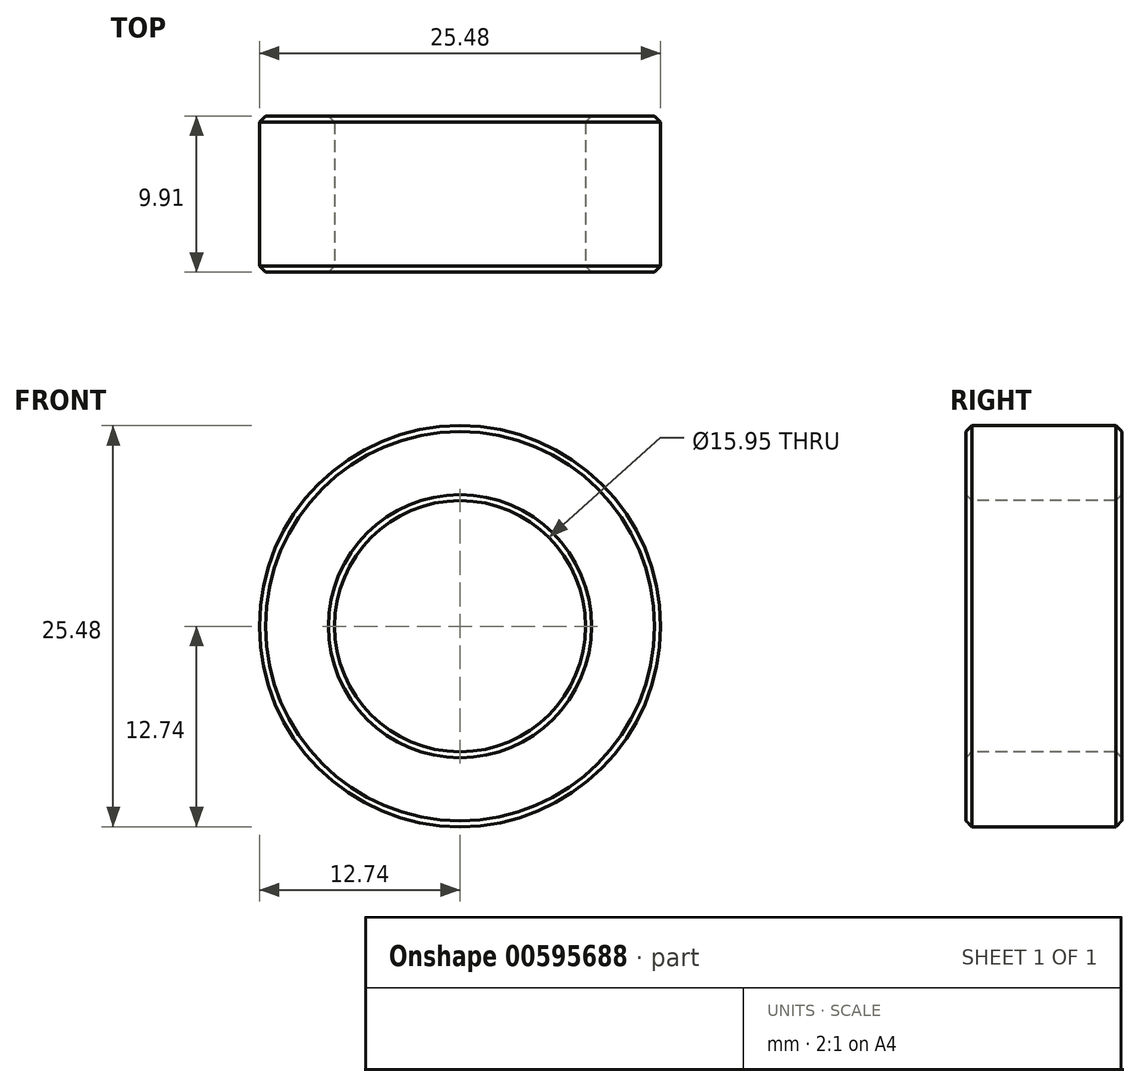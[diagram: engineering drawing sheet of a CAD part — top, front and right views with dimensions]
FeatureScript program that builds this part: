
annotation { "Feature Type Name" : "Feature", "Feature Type Description" : "" }
export const myFeature = defineFeature(function(context is Context, id is Id, definition is map)
    precondition{}
    {
        {
            var Q0;
            Q0=qCreatedBy(makeId("Right.planeOp"),FACE);
            var sketch = newSketch(context, id + "F0", { "sketchPlane" : qUnion([Q0])});
            skLineSegment(sketch, "E0.bottom", {"start": v(0, 7.98) * mm, "end": v(9.9, 7.98) * mm});
            skLineSegment(sketch, "E0.top", {"start": v(0, 12.74) * mm, "end": v(9.9, 12.74) * mm});
            skLineSegment(sketch, "E0.left", {"start": v(0, 7.98) * mm, "end": v(0, 12.74) * mm});
            skLineSegment(sketch, "E0.right", {"start": v(9.9, 7.98) * mm, "end": v(9.9, 12.74) * mm});
            skLineSegment(sketch, "E1", {"start": v(0, 0) * mm, "end": v(6.18, 0) * mm, "construction": true});
            skSolve(sketch);
        }
        {
            var Q0;
            Q0 = qSketchRegion(id + "F0", true);
            var Q1;
            Q1=sQuery(id+"F0.wireOp",EDGE,"E1");
            revolve(context, id + "F1", {"entities" : qUnion([Q0]), "axis" : qUnion([Q1]), "revolveType" : RevolveType.FULL});
        }
        {
            var Q0;
            Q0=makeQuery(id+"F1.opRevolve","SWEPT_FACE",FACE,{"disambiguationData":[OSD([sQuery(id+"F0.wireOp",EDGE,"E0.top")])]});
            var Q1;
            Q1=makeQuery(id+"F1.opRevolve","SWEPT_FACE",FACE,{"disambiguationData":[OSD([sQuery(id+"F0.wireOp",EDGE,"E0.bottom")])]});
            chamfer(context, id + "F2", {"entities" : qUnion([Q0, Q1]), "width" : 0.38 * mm, "tangentPropagation" : true});
        }
    });
